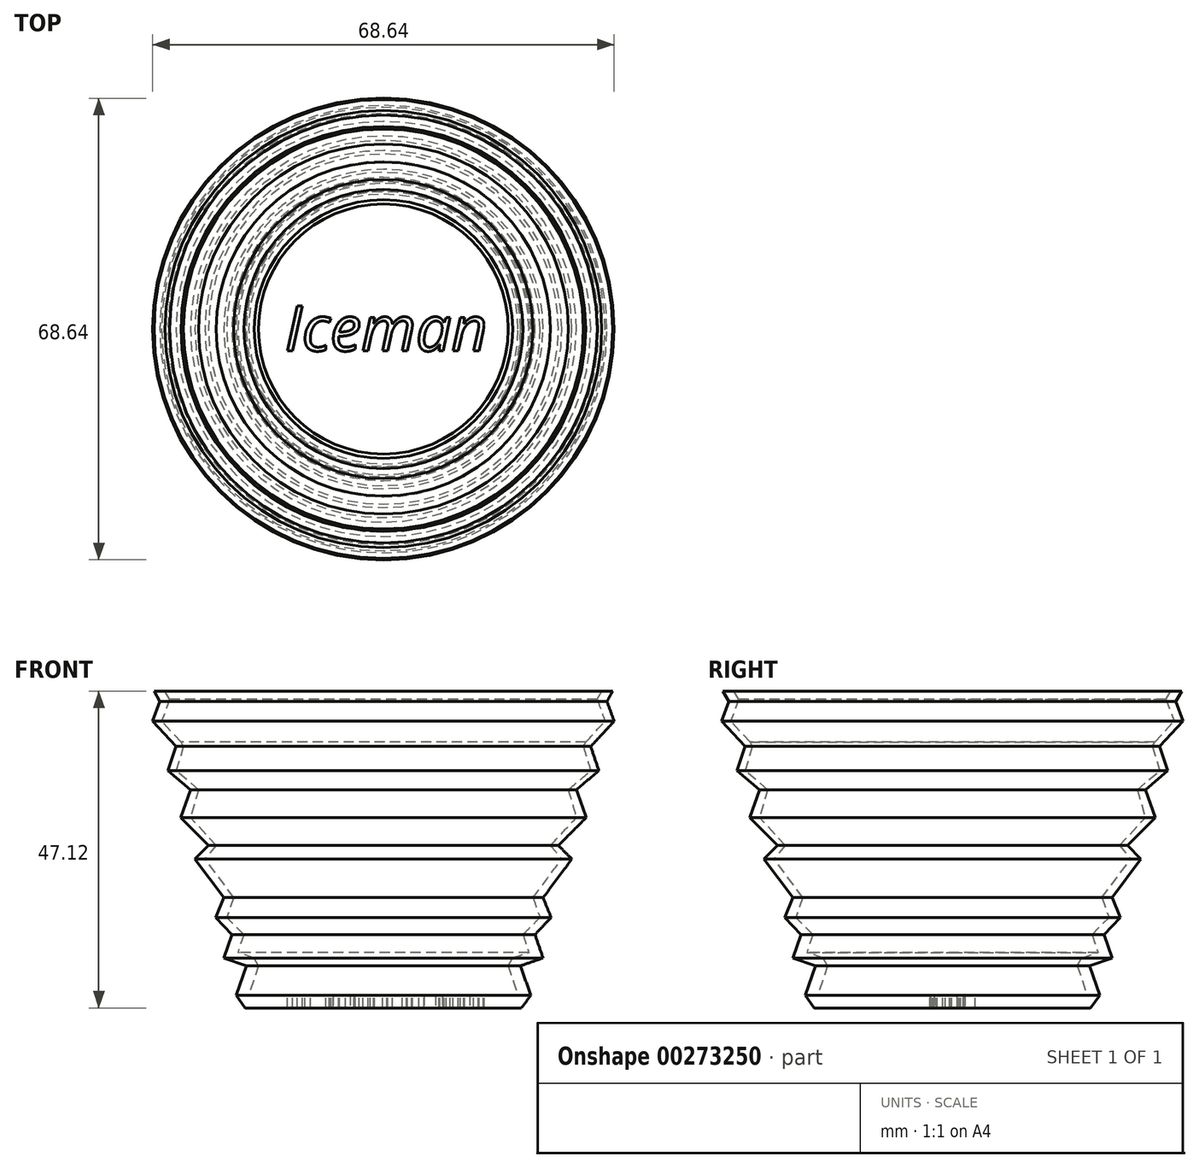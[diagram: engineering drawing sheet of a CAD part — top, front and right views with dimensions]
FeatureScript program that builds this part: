
annotation { "Feature Type Name" : "Feature", "Feature Type Description" : "" }
export const myFeature = defineFeature(function(context is Context, id is Id, definition is map)
    precondition{}
    {
        {
            var Q0;
            Q0=qCreatedBy(makeId("Front.planeOp"),FACE);
            var sketch = newSketch(context, id + "F0", { "sketchPlane" : qUnion([Q0])});
            skLineSegment(sketch, "E0", {"start": v(-34.11, 47.12) * mm, "end": v(-33.25, 45.57) * mm});
            skLineSegment(sketch, "E1", {"start": v(-33.25, 45.57) * mm, "end": v(-34.32, 42.62) * mm});
            skLineSegment(sketch, "E2", {"start": v(-34.32, 42.62) * mm, "end": v(-30.84, 38.88) * mm});
            skLineSegment(sketch, "E3", {"start": v(-30.84, 38.88) * mm, "end": v(-32.05, 35.26) * mm});
            skLineSegment(sketch, "E4", {"start": v(-32.05, 35.26) * mm, "end": v(-28.7, 32.45) * mm});
            skLineSegment(sketch, "E5", {"start": v(-28.7, 32.45) * mm, "end": v(-30.18, 28.3) * mm});
            skLineSegment(sketch, "E6", {"start": v(-30.18, 28.3) * mm, "end": v(-26.03, 24.16) * mm});
            skLineSegment(sketch, "E7", {"start": v(-26.03, 24.16) * mm, "end": v(-28.03, 22.15) * mm});
            skLineSegment(sketch, "E8", {"start": v(-28.03, 22.15) * mm, "end": v(-23.75, 16.4) * mm});
            skLineSegment(sketch, "E9", {"start": v(-23.75, 16.4) * mm, "end": v(-24.96, 13.45) * mm});
            skLineSegment(sketch, "E10", {"start": v(-24.96, 13.45) * mm, "end": v(-22.55, 10.9) * mm});
            skLineSegment(sketch, "E11", {"start": v(-22.55, 10.9) * mm, "end": v(-23.75, 7.43) * mm});
            skLineSegment(sketch, "E12", {"start": v(-23.75, 7.43) * mm, "end": v(-20.4, 6.27) * mm});
            skLineSegment(sketch, "E13", {"start": v(-20.4, 6.27) * mm, "end": v(-21.92, 1.86) * mm});
            skLineSegment(sketch, "E14", {"start": v(-21.92, 1.86) * mm, "end": v(-20.53, 0) * mm});
            skLineSegment(sketch, "E15", {"start": v(-20.53, 0) * mm, "end": v(0, 0) * mm});
            skPoint(sketch, "E16.end.orphan", {"position": v(-19.32, 6.27) * mm});
            skPoint(sketch, "E17.end.orphan", {"position": v(-20.84, 1.86) * mm});
            skLineSegment(sketch, "E18", {"start": v(0, 53.75) * mm, "end": v(0, -3.48) * mm, "construction": true});
            skLineSegment(sketch, "E19", {"start": v(-34.11, 47.12) * mm, "end": v(-32.49, 47.12) * mm});
            skLineSegment(sketch, "E20", {"start": v(-32.49, 47.12) * mm, "end": v(-31.8, 45.87) * mm});
            skLineSegment(sketch, "E21", {"start": v(-31.8, 45.87) * mm, "end": v(-32.98, 42.62) * mm});
            skLineSegment(sketch, "E22", {"start": v(-32.98, 42.62) * mm, "end": v(-30.1, 39.52) * mm});
            skLineSegment(sketch, "E23", {"start": v(-30.1, 39.52) * mm, "end": v(-29.74, 38.88) * mm});
            skLineSegment(sketch, "E24", {"start": v(-29.74, 38.88) * mm, "end": v(-30.84, 35.26) * mm});
            skLineSegment(sketch, "E25", {"start": v(-30.84, 35.26) * mm, "end": v(-27.5, 32.45) * mm});
            skLineSegment(sketch, "E26", {"start": v(-27.5, 32.45) * mm, "end": v(-28.7, 28.3) * mm});
            skLineSegment(sketch, "E27", {"start": v(-28.7, 28.3) * mm, "end": v(-24.85, 24.16) * mm});
            skLineSegment(sketch, "E28", {"start": v(-24.85, 24.16) * mm, "end": v(-26.54, 22.15) * mm});
            skLineSegment(sketch, "E29", {"start": v(-26.54, 22.15) * mm, "end": v(-22.25, 16.4) * mm});
            skLineSegment(sketch, "E30", {"start": v(-22.25, 16.4) * mm, "end": v(-23.3, 13.45) * mm});
            skLineSegment(sketch, "E31", {"start": v(-23.3, 13.45) * mm, "end": v(-20.76, 10.9) * mm});
            skLineSegment(sketch, "E32", {"start": v(-20.76, 10.9) * mm, "end": v(-21.65, 8.24) * mm});
            skLineSegment(sketch, "E33", {"start": v(-21.65, 8.24) * mm, "end": v(-19.22, 7.43) * mm});
            skLineSegment(sketch, "E34", {"start": v(-19.22, 7.43) * mm, "end": v(-18.58, 6.27) * mm});
            skLineSegment(sketch, "E35", {"start": v(-18.58, 6.27) * mm, "end": v(-20.05, 1.86) * mm});
            skLineSegment(sketch, "E36", {"start": v(-20.05, 1.86) * mm, "end": v(0, 1.86) * mm});
            skLineSegment(sketch, "E37", {"start": v(0, 1.86) * mm, "end": v(0, 0) * mm});
            skSolve(sketch);
        }
        {
            var Q0;
            Q0 = qSketchRegion(id + "F0", true);
            var Q1;
            Q1=sQuery(id+"F0.wireOp",EDGE,"E18");
            revolve(context, id + "F1", {"entities" : qUnion([Q0]), "axis" : qUnion([Q1]), "revolveType" : RevolveType.FULL});
        }
        {
            var Q0;
            Q0=makeQuery(id+"F1.opRevolve","SWEPT_FACE",FACE,{"disambiguationData":[OSD([sQuery(id+"F0.wireOp",EDGE,"E36")])]});
            var sketch = newSketch(context, id + "F2", { "sketchPlane" : qUnion([Q0])});
            skText(sketch, "E38", { "text": "Iceman\n", "fontName": "OpenSans-Italic.ttf"});
            const initialGuessF2  = {"E38": [-0.01465, -0.00325, 1, 0, 0.00672]};
            skSetInitialGuess(sketch, initialGuessF2);
            skSolve(sketch);
        }
        {
            var Q0;
            Q0 = qSketchRegion(id + "F2", true);
            extrude(context, id + "F3", {"entities" : qUnion([Q0]), "operationType" : NewBodyOperationType.REMOVE, "endBound" : BoundingType.THROUGH_ALL, "oppositeDirection" : true, "depth" : 25.4 * mm});
        }
    });
